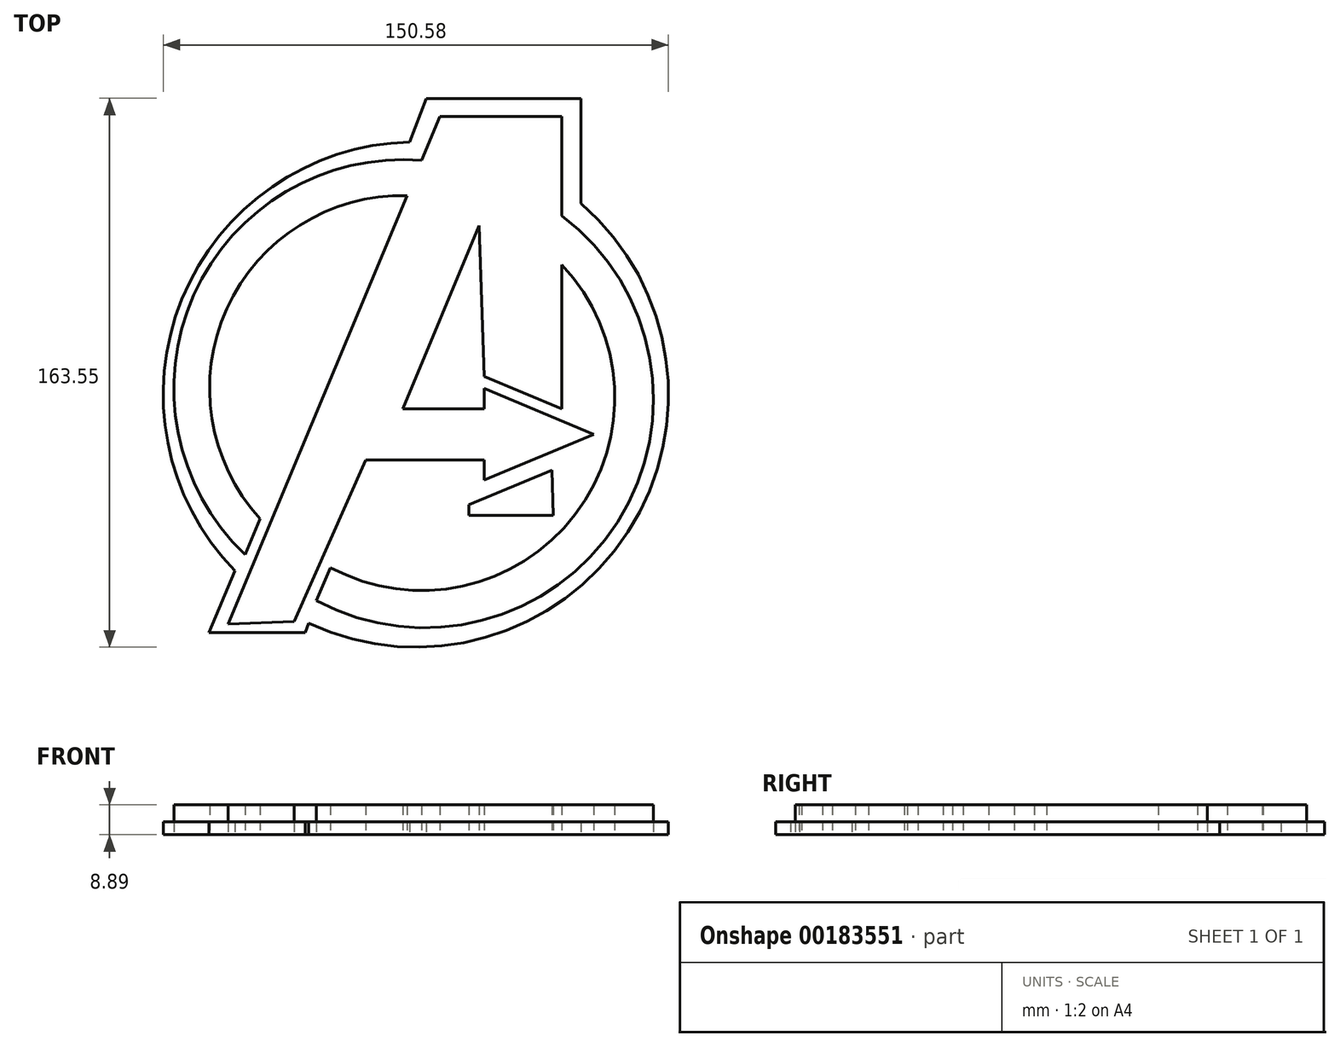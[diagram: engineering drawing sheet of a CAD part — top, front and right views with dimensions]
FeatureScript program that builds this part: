
annotation { "Feature Type Name" : "Feature", "Feature Type Description" : "" }
export const myFeature = defineFeature(function(context is Context, id is Id, definition is map)
    precondition{}
    {
        {
            var Q0;
            Q0=qCreatedBy(makeId("Top.planeOp"),FACE);
            var sketch = newSketch(context, id + "F0", { "sketchPlane" : qUnion([Q0])});
            skArc(sketch, "E0", {"start": v(1.28, 57.52) * mm, "mid": v(-52.38, 23.8) * mm, "end": v(-42.49, -38.8) * mm});
            skArc(sketch, "E1.0", {"start": v(5.64, 67.97) * mm, "mid": v(-62.25, 27.87) * mm, "end": v(-46.94, -49.47) * mm});
            skLineSegment(sketch, "E2", {"start": v(11.12, 81.11) * mm, "end": v(5.64, 67.97) * mm});
            skLineSegment(sketch, "E3", {"start": v(-51.96, -70.14) * mm, "end": v(-32.36, -69.42) * mm});
            skLineSegment(sketch, "E4", {"start": v(-32.36, -69.42) * mm, "end": v(-11.04, -21.22) * mm});
            skLineSegment(sketch, "E5", {"start": v(-11.04, -21.22) * mm, "end": v(24.27, -21.22) * mm});
            skLineSegment(sketch, "E6", {"start": v(24.27, -21.22) * mm, "end": v(24.27, -27.22) * mm});
            skLineSegment(sketch, "E7", {"start": v(24.27, 0) * mm, "end": v(24.27, -6) * mm});
            skLineSegment(sketch, "E8", {"start": v(24.27, -6) * mm, "end": v(0, -6) * mm});
            skLineSegment(sketch, "E9", {"start": v(0, -6) * mm, "end": v(22.75, 48.56) * mm});
            skLineSegment(sketch, "E10", {"start": v(22.75, 48.56) * mm, "end": v(24.27, 3.65) * mm});
            skLineSegment(sketch, "E11", {"start": v(24.27, 3.65) * mm, "end": v(47.4, -6) * mm});
            skLineSegment(sketch, "E12", {"start": v(47.4, -6) * mm, "end": v(47.4, 36.95) * mm});
            skLineSegment(sketch, "E13", {"start": v(47.4, 81.11) * mm, "end": v(11.12, 81.11) * mm});
            skLineSegment(sketch, "E14", {"start": v(24.27, 0) * mm, "end": v(56.9, -13.6) * mm});
            skLineSegment(sketch, "E15", {"start": v(56.9, -13.6) * mm, "end": v(24.27, -27.22) * mm});
            skLineSegment(sketch, "E16", {"start": v(-42.49, -38.8) * mm, "end": v(-46.94, -49.47) * mm});
            skLineSegment(sketch, "E17", {"start": v(-21.5, -53.37) * mm, "end": v(-25.75, -63.15) * mm});
            skLineSegment(sketch, "E18", {"start": v(44.45, -24.39) * mm, "end": v(19.8, -34.67) * mm});
            skLineSegment(sketch, "E19.trimOffspring", {"start": v(1.28, 57.52) * mm, "end": v(-51.96, -70.14) * mm});
            skLineSegment(sketch, "E20.trimOffspring", {"start": v(47.4, 51.52) * mm, "end": v(47.4, 81.11) * mm});
            skArc(sketch, "E21.trimOffspring", {"start": v(-21.5, -53.37) * mm, "mid": v(51.4, -37.55) * mm, "end": v(47.4, 36.95) * mm});
            skArc(sketch, "E22.trimOffspring", {"start": v(-25.75, -63.15) * mm, "mid": v(64.04, -39.77) * mm, "end": v(47.4, 51.52) * mm});
            skPoint(sketch, "E23.end.orphan", {"position": v(-16.5, -3.08) * mm});
            skLineSegment(sketch, "E24", {"start": v(19.8, -34.67) * mm, "end": v(19.8, -37.82) * mm});
            skLineSegment(sketch, "E25", {"start": v(44.45, -24.39) * mm, "end": v(44.9, -37.82) * mm});
            skLineSegment(sketch, "E26", {"start": v(44.9, -37.82) * mm, "end": v(19.8, -37.82) * mm});
            skSolve(sketch);
        }
        {
            var Q0;
            Q0=makeQuery(id+"F0.imprint","IMPRINT",FACE,{"disambiguationData":[TD([[makeQuery(id+"F0.imprint","IMPRINT",EDGE,{"derivedFrom":sQuery(id+"F0.wireOp",EDGE,"E0")}),-1.0]])]});
            var Q1;
            Q1=makeQuery(id+"F0.imprint","IMPRINT",FACE,{"disambiguationData":[TD([[makeQuery(id+"F0.imprint","IMPRINT",EDGE,{"derivedFrom":sQuery(id+"F0.wireOp",EDGE,"E18")}),1.0]])]});
            extrude(context, id + "F1", {"entities" : qUnion([Q0, Q1]), "depth" : 8.9 * mm});
        }
        {
            var Q0;
            Q0=qCreatedBy(makeId("Top.planeOp"),FACE);
            var sketch = newSketch(context, id + "F2", { "sketchPlane" : qUnion([Q0])});
            skArc(sketch, "E27", {"start": v(2.08, 73.48) * mm, "mid": v(-65.8, 26.6) * mm, "end": v(-49.96, -54.36) * mm});
            skLineSegment(sketch, "E28", {"start": v(2.08, 73.48) * mm, "end": v(7.01, 86.48) * mm});
            skLineSegment(sketch, "E29", {"start": v(7.01, 86.48) * mm, "end": v(53.18, 86.48) * mm});
            skLineSegment(sketch, "E30", {"start": v(53.18, 86.48) * mm, "end": v(53.18, 55.17) * mm});
            skLineSegment(sketch, "E31", {"start": v(-49.96, -54.36) * mm, "end": v(-57.68, -72.73) * mm});
            skLineSegment(sketch, "E32", {"start": v(-57.68, -72.73) * mm, "end": v(-28.97, -72.73) * mm});
            skLineSegment(sketch, "E33", {"start": v(-28.97, -72.73) * mm, "end": v(-28, -69.97) * mm});
            skArc(sketch, "E34.trimOffspring", {"start": v(-28, -69.97) * mm, "mid": v(67.1, -42.76) * mm, "end": v(53.18, 55.17) * mm});
            skSolve(sketch);
        }
        {
            var Q0;
            Q0 = qSketchRegion(id + "F2", true);
            extrude(context, id + "F3", {"entities" : qUnion([Q0]), "depth" : 3.8 * mm});
        }
    });
